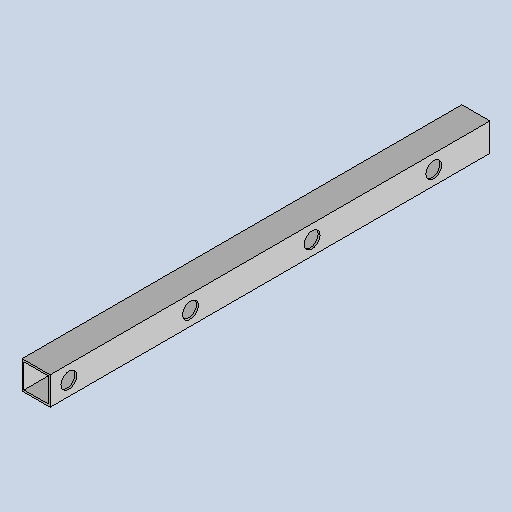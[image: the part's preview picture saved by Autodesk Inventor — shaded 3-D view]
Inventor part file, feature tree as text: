
AUTODESK INVENTOR PART (.ipt)
format: ipt  version: 2025.1 (Build 291241020, 241B)  size: 151,040 bytes
history: native  units: mm
features: extrude x2, sketch x2, projected_geometry x1
ambient origin geometry x8: Origin, YZ Plane, XZ Plane, XY Plane, X Axis, Y Axis, Z Axis, Center Point
bodies: Body1 (feature_tree)
feature tree (5):
  extrude  "Extrusion3"  Depth=30.0mm
  extrude  "Extrusion4"  Depth=2.0mm
  sketch  "Sketch9"  dims[d61=500.0mm d172=30.0mm]
  sketch  "Sketch10"  dims[d173=30.0mm d174=2.0mm d175=470.0mm d176=0.0mm d177=17.0mm d178=17.0mm d179=0.0mm d180=0.0mm d181=30.0mm d182=90.0mm d183=220.0mm d184=350.0mm d185=480.0mm d186=17.0mm]
  projected_geometry  "Projected Loop3"
